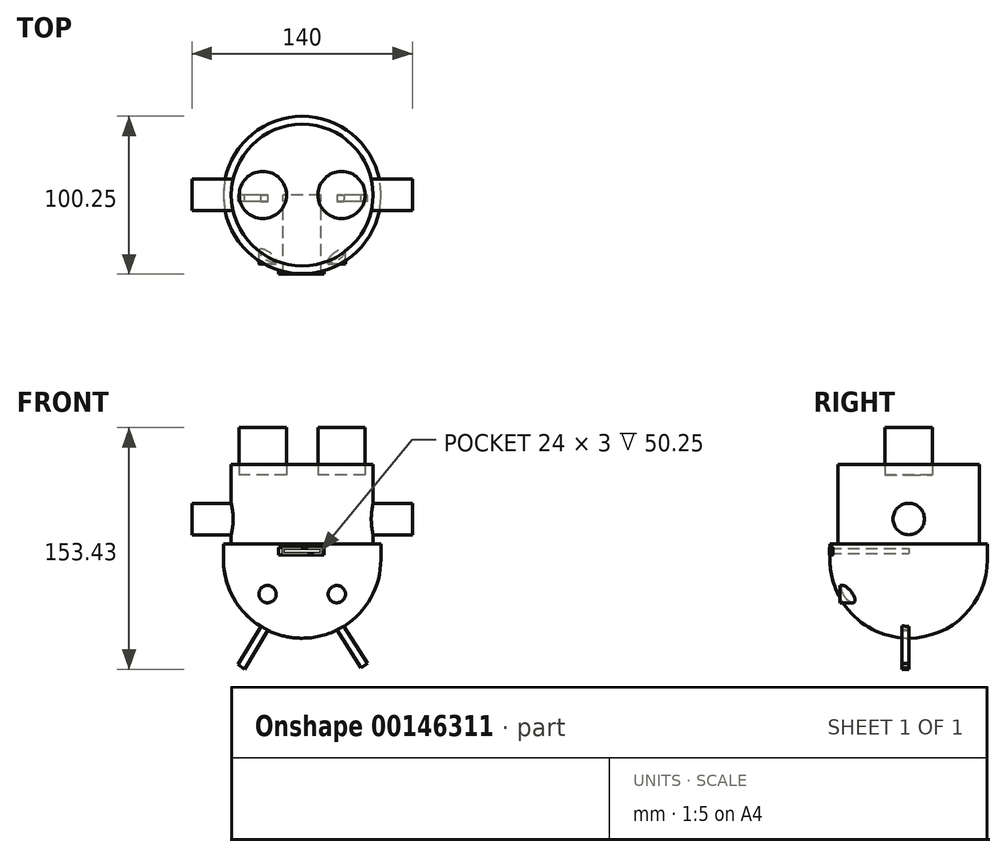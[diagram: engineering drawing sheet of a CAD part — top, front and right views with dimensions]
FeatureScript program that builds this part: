
annotation { "Feature Type Name" : "Feature", "Feature Type Description" : "" }
export const myFeature = defineFeature(function(context is Context, id is Id, definition is map)
    precondition{}
    {
        {
            var Q0;
            Q0=qCreatedBy(makeId("Top.planeOp"),FACE);
            var sketch = newSketch(context, id + "F0", { "sketchPlane" : qUnion([Q0])});
            skCircle(sketch, "E0", {"center": v(-25, 0) * mm, "radius": 15 * mm});
            skCircle(sketch, "E1", {"center": v(25, 0) * mm, "radius": 15 * mm});
            skSolve(sketch);
        }
        {
            var Q0;
            Q0=qCreatedBy(makeId("Top.planeOp"),FACE);
            var sketch = newSketch(context, id + "F1", { "sketchPlane" : qUnion([Q0])});
            skCircle(sketch, "E2", {"center": v(0, 0) * mm, "radius": 45 * mm});
            skSolve(sketch);
        }
        {
            var Q0;
            Q0=qCreatedBy(makeId("Top.planeOp"),FACE);
            var sketch = newSketch(context, id + "F2", { "sketchPlane" : qUnion([Q0])});
            skCircle(sketch, "E3", {"center": v(0, 0) * mm, "radius": 50 * mm});
            skSolve(sketch);
        }
        {
            var Q0;
            Q0 = qSketchRegion(id + "F0", true);
            extrude(context, id + "F3", {"entities" : qUnion([Q0]), "depth" : 30 * mm});
        }
        {
            var Q0;
            Q0=makeQuery(id+"F1.imprint","IMPRINT",FACE,{"disambiguationData":[TD([[makeQuery(id+"F1.imprint","IMPRINT",EDGE,{"derivedFrom":sQuery(id+"F1.wireOp",EDGE,"E2")}),1.0]])]});
            extrude(context, id + "F4", {"entities" : qUnion([Q0]), "oppositeDirection" : true, "depth" : 50 * mm, "hasSecondDirection" : true, "secondDirectionOppositeDirection" : false, "secondDirectionDepth" : 6.5 * mm});
        }
        {
            var Q0;
            Q0=makeQuery(id+"F2.imprint","IMPRINT",FACE,{"disambiguationData":[TD([[makeQuery(id+"F2.imprint","IMPRINT",EDGE,{"derivedFrom":sQuery(id+"F2.wireOp",EDGE,"E3")}),1.0]])]});
            extrude(context, id + "F5", {"entities" : qUnion([Q0]), "operationType" : NewBodyOperationType.ADD, "oppositeDirection" : true, "depth" : 53.75 * mm, "hasSecondDirection" : true, "secondDirectionOppositeDirection" : true, "secondDirectionDepth" : 44 * mm});
        }
        {
            var Q0;
            Q0=qCreatedBy(makeId("Right.planeOp"),FACE);
            var sketch = newSketch(context, id + "F6", { "sketchPlane" : qUnion([Q0])});
            skCircle(sketch, "E4", {"center": v(0, -28) * mm, "radius": 10 * mm});
            skSolve(sketch);
        }
        {
            var Q0;
            Q0 = qSketchRegion(id + "F6", true);
            extrude(context, id + "F7", {"entities" : qUnion([Q0]), "operationType" : NewBodyOperationType.ADD, "depth" : 70 * mm});
        }
        {
            var Q0;
            Q0=qCreatedBy(makeId("Right.planeOp"),FACE);
            var sketch = newSketch(context, id + "F8", { "sketchPlane" : qUnion([Q0])});
            skCircle(sketch, "E5", {"center": v(0, -28) * mm, "radius": 10 * mm});
            skSolve(sketch);
        }
        {
            var Q0;
            Q0 = qSketchRegion(id + "F8", true);
            extrude(context, id + "F9", {"entities" : qUnion([Q0]), "operationType" : NewBodyOperationType.ADD, "oppositeDirection" : true, "depth" : 70 * mm});
        }
        {
            var Q0;
            Q0=qCreatedBy(makeId("Front.planeOp"),FACE);
            var sketch = newSketch(context, id + "F10", { "sketchPlane" : qUnion([Q0])});
            skArc(sketch, "E6", {"start": v(-50, -53.75) * mm, "mid": v(0, -103.75) * mm, "end": v(50, -53.75) * mm});
            skPoint(sketch, "E7", {"position": v(-50, -53.75) * mm});
            skLineSegment(sketch, "E8", {"start": v(-50, -53.75) * mm, "end": v(50, -53.75) * mm});
            skLineSegment(sketch, "E9", {"start": v(0, -53.75) * mm, "end": v(0, -103.75) * mm});
            skSolve(sketch);
        }
        {
            var Q0;
            {var subQ3=sQuery(id+"F10.wireOp",EDGE,"E9");Q0=makeQuery(id+"F10.imprint","IMPRINT",FACE,{"disambiguationData":[TD([[makeQuery(id+"F10.imprint","IMPRINT",EDGE,{"derivedFrom":subQ3}),1.0]])]});}
            var Q1;
            Q1=sQuery(id+"F10.wireOp",EDGE,"E9");
            revolve(context, id + "F11", {"operationType" : NewBodyOperationType.ADD, "entities" : qUnion([Q0]), "axis" : qUnion([Q1]), "revolveType" : RevolveType.FULL});
        }
        {
            var Q0;
            Q0=qCreatedBy(makeId("Front.planeOp"),FACE);
            var sketch = newSketch(context, id + "F12", { "sketchPlane" : qUnion([Q0])});
            skCircle(sketch, "E10", {"center": v(22, -75.75) * mm, "radius": 5.5 * mm});
            skCircle(sketch, "E11", {"center": v(-22, -75.75) * mm, "radius": 5.5 * mm});
            skSolve(sketch);
        }
        {
            var Q0;
            Q0 = qSketchRegion(id + "F12", true);
            extrude(context, id + "F13", {"entities" : qUnion([Q0]), "operationType" : NewBodyOperationType.ADD, "depth" : 43.75 * mm});
        }
        {
            var Q0;
            Q0=qCreatedBy(makeId("Front.planeOp"),FACE);
            var sketch = newSketch(context, id + "F14", { "sketchPlane" : qUnion([Q0])});
            skLineSegment(sketch, "E12", {"start": v(41.36, -119.85) * mm, "end": v(37.27, -122.74) * mm});
            skLineSegment(sketch, "E13", {"start": v(-36.73, -123.43) * mm, "end": v(-40.64, -120.32) * mm});
            skLineSegment(sketch, "E14", {"start": v(25.95, -95.29) * mm, "end": v(21.59, -97.74) * mm});
            skLineSegment(sketch, "E15", {"start": v(-25.58, -95.54) * mm, "end": v(-21.5, -98.43) * mm});
            skLineSegment(sketch, "E16", {"start": v(-21.5, -98.43) * mm, "end": v(-36.73, -123.43) * mm});
            skLineSegment(sketch, "E17", {"start": v(37.27, -122.74) * mm, "end": v(21.59, -97.74) * mm});
            skLineSegment(sketch, "E18", {"start": v(41.36, -119.85) * mm, "end": v(25.95, -95.29) * mm});
            skLineSegment(sketch, "E19", {"start": v(-25.58, -95.54) * mm, "end": v(-40.64, -120.32) * mm});
            skSolve(sketch);
        }
        {
            var Q0;
            Q0 = qSketchRegion(id + "F14", true);
            extrude(context, id + "F15", {"entities" : qUnion([Q0]), "operationType" : NewBodyOperationType.ADD, "depth" : 4.25 * mm});
        }
        {
            var Q0;
            Q0=qCreatedBy(makeId("Front.planeOp"),FACE);
            var sketch = newSketch(context, id + "F16", { "sketchPlane" : qUnion([Q0])});
            skLineSegment(sketch, "E20", {"start": v(13.88, -51) * mm, "end": v(-15.12, -51) * mm});
            skLineSegment(sketch, "E21", {"start": v(-15.12, -51) * mm, "end": v(-15.12, -46) * mm});
            skLineSegment(sketch, "E22", {"start": v(-15.12, -46) * mm, "end": v(13.88, -46) * mm});
            skLineSegment(sketch, "E23", {"start": v(13.88, -46) * mm, "end": v(13.88, -51) * mm});
            skSolve(sketch);
        }
        {
            var Q0;
            Q0 = qSketchRegion(id + "F16", true);
            extrude(context, id + "F17", {"entities" : qUnion([Q0]), "operationType" : NewBodyOperationType.ADD, "depth" : 50.25 * mm});
        }
        {
            var Q0;
            Q0=qCreatedBy(makeId("Front.planeOp"),FACE);
            var sketch = newSketch(context, id + "F18", { "sketchPlane" : qUnion([Q0])});
            skLineSegment(sketch, "E24", {"start": v(12, -49.8) * mm, "end": v(-12, -49.8) * mm});
            skLineSegment(sketch, "E25", {"start": v(-12, -49.8) * mm, "end": v(-12, -46.8) * mm});
            skLineSegment(sketch, "E26", {"start": v(-12, -46.8) * mm, "end": v(12, -46.8) * mm});
            skLineSegment(sketch, "E27", {"start": v(12, -46.8) * mm, "end": v(12, -49.8) * mm});
            skSolve(sketch);
        }
        {
            var Q0;
            Q0 = qSketchRegion(id + "F18", true);
            extrude(context, id + "F19", {"entities" : qUnion([Q0]), "operationType" : NewBodyOperationType.REMOVE, "depth" : 52 * mm});
        }
    });
